# Revit family: FA_АктивныйМолниеприемник_FOREND EU-M_91888-1_EZETEK
name_source: partatom
category: Системы пожарной сигнализации
revit_build: Autodesk Revit 2017 (Build: 20170118_1100(x64)
units: mm (PartAtom-declared; Revit-internal decimal feet)

## family parameters
Всегда вертикально = Да
На основе рабочей плоскости = Нет
Общий = Да
При загрузке вырезать с полостями = Нет
Размер круглого соединителя = Использовать радиус
Сохранять ориентацию аннотаций = Нет
Тип детали = Нормальный
Точка расчета площади = Нет

## types (1)
- АктивныйМолниеприемник_FOREND EU-M_91888-1
    ADSK_Версия Revit = 2017
    ADSK_Единица измерения = шт.
    ADSK_Завод-изготовитель = Ezetek
    ADSK_Код изделия = 91888-1
    ADSK_Количество = 1
    ADSK_Марка = 91888-1
    ADSK_Масса = 3.2
    ADSK_Масса_Текст = 3.20
    ADSK_Материал = BIMLIB_Сталь_Нержавеющая_EZETEK
    ADSK_Наименование = Активный молниеприемник FOREND EU-M
    ADSK_Обозначение = 91888-1
    URL = https://ezetek.ru
    Группа модели = Активная молниезащита
    Изготовитель = Ezetek
    Описание = Активный молниеприемник FOREND EU-M состоит из корпуса, генератора ионов и соединительной муфты. Корпус из нержавеющей стали обеспечивает надежную защиту молниеприемника от коррозии на срок не менее 25 лет. Генератор ионов размещен внутри корпуса в дополнительном кожухе для обеспечения герметичности. Во время грозы генератор вырабатывает статические заряды, которые поддерживают ионизацию воздуха вокруг молниеприемника и создают благоприятные условия для начала формирования встречного лидера молнии. Соединительная муфта применяется для подключения токоотвода к активному молниеприемнику и заземляющему устройству.

Молниеприемник и все металлические объекты на кровле должны быть соединены с заземляющим устройством. Модульно-штыревое заземление для активной молниезащиты просто в исполнении - нет необходимости монтировать контур заземления вокруг здания. Степень защиты молниеприемника – IP 65, диапазон рабочих температур - от -40 °С до +120 °С. Радиус зоны защиты активного молниеприемника FOREND EU-M зависит от высоты установки молниеприемника и категории молниезащиты объекта.
